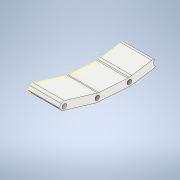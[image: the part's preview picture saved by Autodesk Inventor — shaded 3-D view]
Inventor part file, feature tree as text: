
AUTODESK INVENTOR PART (.ipt)
format: ipt  version: 2020 (Build 240168000, 168)  size: 311,808 bytes
history: native  units: in
note: dims shown in document units (in); Inventor stores cm internally (conversion verified against a paired STEP export)
features: projected_geometry x4, extrude x3, sketch x3
ambient origin geometry x8: Origin, YZ Plane, XZ Plane, XY Plane, X Axis, Y Axis, Z Axis, Center Point
bodies: Solid2 (feature_tree), Solid1 (feature_tree)
feature tree (10):
  extrude  "right side 5mm extension"  Depth=0.1969in TaperAngle=0.0deg
  extrude  "left side 5mm extension"  [1 undecoded]
  extrude  "delete top fin"  [1 undecoded]
  sketch  "Sketch5"
  projected_geometry  "Projected Loop1"
  sketch  "Sketch3"  dims[d5=0.1969in d6=0.0in d7=0.1969in d8=0.0in]
  projected_geometry  "Projected Loop2"
  sketch  "Sketch4"  dims[d9=0.1969in d10=0.0in]
  projected_geometry  "Projected Loop3"
  projected_geometry  "Projected Loop4"
note: 2 required parameter values undecoded (feature->parameter linkage not recoverable at this tier; creation-order binding heuristic only, values carry confidence <= 0.55)
